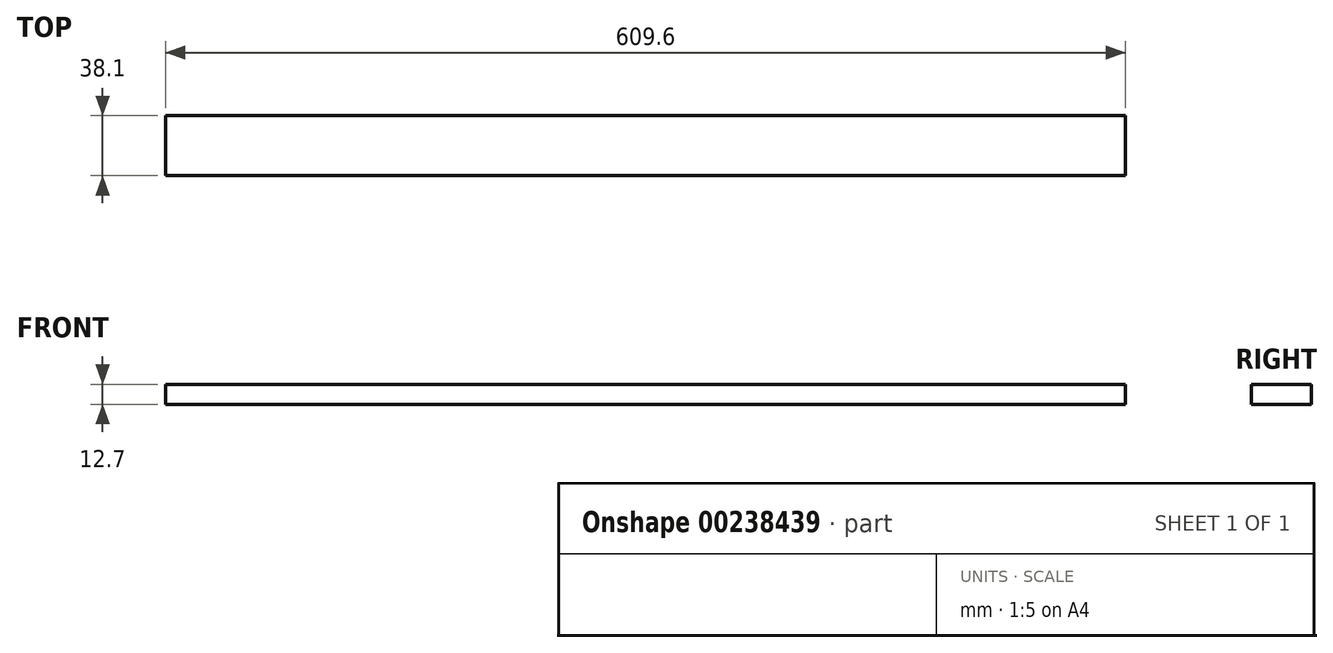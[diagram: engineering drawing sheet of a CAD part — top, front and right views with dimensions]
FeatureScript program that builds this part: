
annotation { "Feature Type Name" : "Feature", "Feature Type Description" : "" }
export const myFeature = defineFeature(function(context is Context, id is Id, definition is map)
    precondition{}
    {
        {
            var Q0;
            Q0=qCreatedBy(makeId("Top.planeOp"),FACE);
            var sketch = newSketch(context, id + "F0", { "sketchPlane" : qUnion([Q0])});
            skLineSegment(sketch, "E0.bottom", {"start": v(-326.65, -115.7) * mm, "end": v(282.95, -115.7) * mm});
            skLineSegment(sketch, "E0.top", {"start": v(-326.65, -153.8) * mm, "end": v(282.95, -153.8) * mm});
            skLineSegment(sketch, "E0.left", {"start": v(-326.65, -115.7) * mm, "end": v(-326.65, -153.8) * mm});
            skLineSegment(sketch, "E0.right", {"start": v(282.95, -115.7) * mm, "end": v(282.95, -153.8) * mm});
            skSolve(sketch);
        }
        {
            var Q0;
            Q0=makeQuery(id+"F0.imprint","IMPRINT",FACE,{"disambiguationData":[TD([[makeQuery(id+"F0.imprint","IMPRINT",EDGE,{"derivedFrom":sQuery(id+"F0.wireOp",EDGE,"E0.bottom")}),-1.0]])]});
            extrude(context, id + "F1", {"entities" : qUnion([Q0]), "depth" : 12.7 * mm});
        }
    });
